# Revit family: Dedicated_Outdoor_Air_System_-_Applied Air_-_FAP
name_source: partatom
category: Attrezzatura meccanica
revit_build: Autodesk Revit 2013 (Build: 20120221_2030)
units: mm (PartAtom-declared; Revit-internal decimal feet)

## types (2) — shared parameters
B = 6' - 10"
CADworks URL = http://www.CADworks.net
Codice assieme = D3050200
Coil Face Area = 36.7 SF
Condensate Drain Radius = 0' - 0 3/4"
Control Cabinet Access Door Width = 1' - 11 7/16"
Cooling Coil Radius = 0' - 1 1/4"
D = 5' - 8"
Descrizione = Dedicated Outdoor Air System
FAP Material = Steel - Applied Air Metal - Series 400 - Galvanized
Fan Blade Center = 2' - 11"
Fan Blade Offset = 2' - 0 5/8"
Fan Diameter = 2' - 1 1/2"
Fan Speed (RPM) = 1140
Frequency = 60 Hz
G = 5' - 10"
Gas Connection Radius = 0' - 0 3/8"
Gas Inlet Horizontal Offset = 1' - 6 1/16"
Gas Inlet Vertical Offset = 2' - 1"
H = 0' - 3 1/16"
J = 0' - 6 3/4"
K = 2' - 1 11/16"
L = 1' - 8 3/4"
Louver Distance = 0' - 2 7/8"
M = 3' - 10"
Maximum Air Flow = 9500 CFM
Maximum Input = 200000.0 Btu/h
Maximum Output = 160000.0 Btu/h
Minimum Air Flow = 1500 CFM
Minimum Input = 6000.0 Btu/h
Modello = 40/20
Nominal Height = 4' - 2"
Nominal Length = 27' - 5"
Nominal Width = 6' - 8"
Number of Coils = 2
Number of Compressors = 2
Number of Fans = 2
Number of Motors = 2
Number of Poles = 3
Number of Rows = 4
P = 3' - 4"
Phase = 3
Product URL = http://www.appliedair.com
Produttore = Applied Air
Prospetto di default = 0' - 0"
Refrigerant Type = R410A
Return Air Flow Height = 1' - 8"
Series = FAP
Tall Condenser Grille Width = 1' - 1"
Total Cooling Capacity = 301260.0 Btu/h
Type Compressor = Scroll
Type Filter = (4) 20x20 and (2) 20x25
URL = http://www.appliedair.com
Unit Weight = 6879.00 lb
Voltage = 480 V

## type names (no varying parameters)
- Dedicated_Outdoor_Air_System_-_Applied Air_-_FAP
- uta sara e chiara

## geometry (parser evidence)
native form markers: Blend x4, Sweep x2
no freeform markers — native parametric forms only
